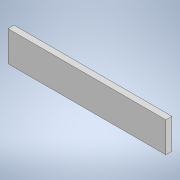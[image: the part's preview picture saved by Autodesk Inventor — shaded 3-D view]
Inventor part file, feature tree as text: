
AUTODESK INVENTOR PART (.ipt)
format: ipt  version: 2021 (Build 250183000, 183)  size: 92,672 bytes
history: native  units: mm
features: other x1, extrude x1, sketch x1
ambient origin geometry x8: Origin, YZ Plane, XZ Plane, XY Plane, X Axis, Y Axis, Z Axis, Center Point
bodies: Body1 (feature_tree)
feature tree (3):
  other  "ソリッド1"
  extrude  "押し出し1"  Depth=1000.0mm
  sketch  "スケッチ1"
